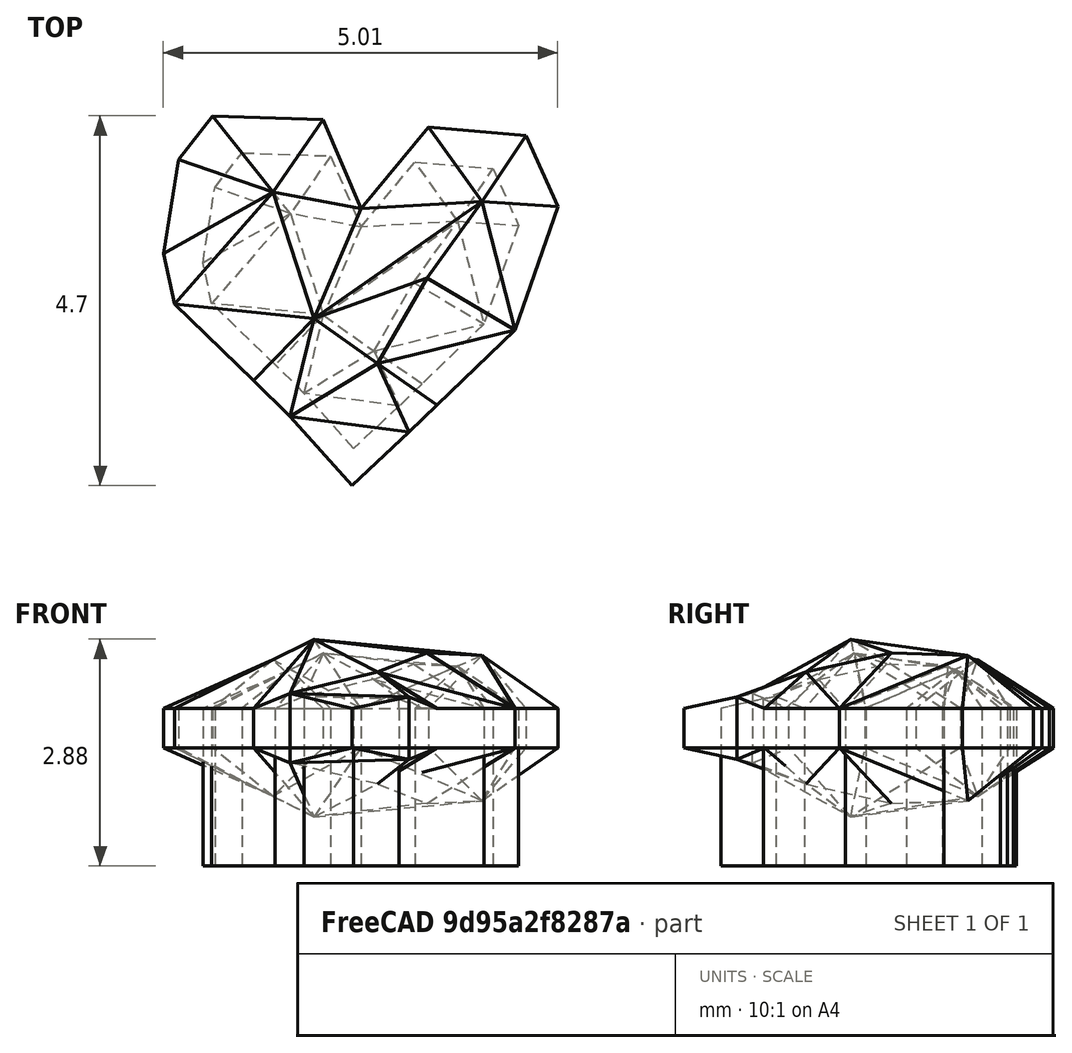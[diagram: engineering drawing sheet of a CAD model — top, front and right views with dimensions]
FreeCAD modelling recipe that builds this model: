
FCSTD DOCUMENT  (FreeCAD 0.20RUnknown)
Label: heart
License: All rights reserved
LicenseURL: http://en.wikipedia.org/wiki/All_rights_reserved
objects: Part::Feature×5, PartDesign::FeatureBase×3, PartDesign::Body×3, Mesh::Feature×2, Sketcher::SketchObject×2, PartDesign::Pad×2, PartDesign::SubShapeBinder×1, Part::Mirroring×1, PartDesign::Boolean×1
note: 20 computed .brp shape members not serialized (recipe doc carries the construction recipe); baked Part::Feature solids carry a one-line shape summary decoded from their .brp

FEATURE [Mesh::Feature] heart_poly_solid
FEATURE [Part::Feature] heart_poly_solid001
  shape: bbox 5.011 x 4.692 x 0.8774 mm, 41 faces, 0 solids (baked)
FEATURE [Part::Feature] heart_poly_solid001_solid  label="heart_poly_solid001 (Solid)"
  shape: bbox 5.011 x 4.692 x 0.8774 mm, 41 faces (baked)
FEATURE [PartDesign::FeatureBase] BaseFeature
  BaseFeature = -> heart_poly_solid001_solid
FEATURE [PartDesign::SubShapeBinder] Binder
  BindCopyOnChange = 0
  BindMode = 0
  ClaimChildren = false
  Context = -> Body [Binder.]
  Fuse = false
  MakeFace = true
  OffsetFill = false
  OffsetIntersection = false
  OffsetJoinType = 0
  OffsetOpenResult = false
  PartialLoad = false
  Relative = true
  Support = -> [heart_poly_solid001_solid]
  _Version = 2
FEATURE [Sketcher::SketchObject] Sketch
  ExternalGeometry = -> [BaseFeature]
  FullyConstrained = true
  MapMode = 5
  Support = -> [XY_Plane]
  sketch-geometry (15):
    g0: LineSegment StartX=-0.114772 StartY=-2.34626 StartZ=0 EndX=-0.898591 EndY=-1.47426 EndZ=0
    g1: LineSegment StartX=-0.898591 StartY=-1.47426 StartZ=0 EndX=-1.36077 EndY=-1.01687 EndZ=0
    g2: LineSegment StartX=-1.36077 StartY=-1.01687 StartZ=0 EndX=-2.36956 EndY=-0.0446064 EndZ=0
    g3: LineSegment StartX=-2.36956 StartY=-0.0446064 StartZ=0 EndX=-2.50731 EndY=0.598821 EndZ=0
    g4: LineSegment StartX=-2.50731 StartY=0.598821 StartZ=0 EndX=-2.31933 EndY=1.79492 EndZ=0
    g5: LineSegment StartX=-2.31933 StartY=1.79492 StartZ=0 EndX=-1.88677 EndY=2.34557 EndZ=0
    g6: LineSegment StartX=-1.88677 StartY=2.34557 StartZ=0 EndX=-0.480936 EndY=2.29776 EndZ=0
    g7: LineSegment StartX=-0.480936 StartY=2.29776 StartZ=0 EndX=-0.000227809 EndY=1.16775 EndZ=0
    g8: LineSegment StartX=-0.000227809 StartY=1.16775 StartZ=0 EndX=0.860947 EndY=2.20207 EndZ=0
    g9: LineSegment StartX=0.860947 StartY=2.20207 StartZ=0 EndX=2.09803 EndY=2.09499 EndZ=0
    g10: LineSegment StartX=2.09803 StartY=2.09499 StartZ=0 EndX=2.50356 EndY=1.19281 EndZ=0
    g11: LineSegment StartX=2.50356 StartY=1.19281 StartZ=0 EndX=1.95514 EndY=-0.370281 EndZ=0
    g12: LineSegment StartX=1.95514 StartY=-0.370281 StartZ=0 EndX=0.967688 EndY=-1.32256 EndZ=0
    g13: LineSegment StartX=0.967688 StartY=-1.32256 StartZ=0 EndX=0.608669 EndY=-1.67147 EndZ=0
    g14: LineSegment StartX=0.608669 StartY=-1.67147 StartZ=0 EndX=-0.114772 EndY=-2.34626 EndZ=0
  constraints (30):
    c: Coincident(g-17,g0)
    c: Coincident(g0,g-17)
    c: Coincident(g0,g1)
    c: Coincident(g1,g-16)
    c: Coincident(g1,g2)
    c: Coincident(g2,g-15)
    c: Coincident(g2,g3)
    c: Coincident(g3,g-14)
    c: Coincident(g3,g4)
    c: Coincident(g4,g-13)
    c: Coincident(g4,g5)
    c: Coincident(g5,g-12)
    c: Coincident(g5,g6)
    c: Coincident(g6,g-11)
    c: Coincident(g6,g7)
    c: Coincident(g7,g-10)
    c: Coincident(g7,g8)
    c: Coincident(g8,g-9)
    c: Coincident(g8,g9)
    c: Coincident(g9,g-8)
    c: Coincident(g9,g10)
    c: Coincident(g10,g-7)
    c: Coincident(g10,g11)
    c: Coincident(g11,g-6)
    c: Coincident(g11,g12)
    c: Coincident(g12,g-5)
    c: Coincident(g12,g13)
    c: Coincident(g13,g-4)
    c: Coincident(g13,g14)
    c: Coincident(g14,g0)
FEATURE [PartDesign::Pad] Pad
  BaseFeature = -> BaseFeature
  Direction = (0,0,1)
  Length = 0.5
  Length2 = 10
  Profile = -> Sketch
  ReferenceAxis = -> Sketch [N_Axis]
  Reversed = true
  Type = 0
FEATURE [Part::Feature] heart_poly_solid001_solid001  label="heart_mirrored_part"
  shape: bbox 5.011 x 4.692 x 0.8774 mm, 41 faces (baked)
FEATURE [Part::Mirroring] Part__Mirroring  label="heart_mirrored_part (Mirror #1)"
  Base = (0,0,0)
  Normal = (0,0,1)
  Placement = pos=(0,0,-0.5) rot=(0,0,1;0rad)
  Source = -> heart_poly_solid001_solid001
FEATURE [PartDesign::FeatureBase] BaseFeature001
  BaseFeature = -> Part__Mirroring
FEATURE [PartDesign::Body] Body001
  BaseFeature = -> Part__Mirroring
  Group = -> [BaseFeature001]
  Origin = -> Origin001
  Placement = pos=(0,0,-0.5) rot=(0,0,1;0rad)
  Tip = -> BaseFeature001
FEATURE [Mesh::Feature] heart_poly_solid002  label="heart_poly_solid_scaled"
FEATURE [Part::Feature] heart_poly_solid002001  label="heart_poly_solid_scaled_shape"
  shape: bbox 4.009 x 3.753 x 0.702 mm, 41 faces, 0 solids (baked)
FEATURE [Part::Feature] heart_poly_solid002001_solid  label="heart_poly_solid_scaled_shape (Solid)"
  shape: bbox 4.009 x 3.753 x 0.702 mm, 41 faces (baked)
FEATURE [PartDesign::FeatureBase] BaseFeature002
  BaseFeature = -> heart_poly_solid002001_solid
FEATURE [Sketcher::SketchObject] Sketch001
  ExternalGeometry = -> [BaseFeature002]
  FullyConstrained = true
  MapMode = 5
  Support = -> [XY_Plane]
  sketch-geometry (15):
    g0: LineSegment StartX=-0.000182247 StartY=0.9342 StartZ=0 EndX=0.688757 EndY=1.76166 EndZ=0
    g1: LineSegment StartX=0.688757 StartY=1.76166 StartZ=0 EndX=1.67842 EndY=1.67599 EndZ=0
    g2: LineSegment StartX=1.67842 StartY=1.67599 StartZ=0 EndX=2.00285 EndY=0.954248 EndZ=0
    g3: LineSegment StartX=2.00285 StartY=0.954248 StartZ=0 EndX=1.56411 EndY=-0.296224 EndZ=0
    g4: LineSegment StartX=1.56411 StartY=-0.296224 StartZ=0 EndX=0.77415 EndY=-1.05804 EndZ=0
    g5: LineSegment StartX=0.77415 StartY=-1.05804 StartZ=0 EndX=0.486935 EndY=-1.33717 EndZ=0
    g6: LineSegment StartX=0.486935 StartY=-1.33717 StartZ=0 EndX=-0.0918176 EndY=-1.87701 EndZ=0
    g7: LineSegment StartX=-0.0918176 StartY=-1.87701 StartZ=0 EndX=-0.718873 EndY=-1.17941 EndZ=0
    g8: LineSegment StartX=-0.718873 StartY=-1.17941 StartZ=0 EndX=-1.08861 EndY=-0.813493 EndZ=0
    g9: LineSegment StartX=-1.08861 StartY=-0.813493 StartZ=0 EndX=-1.89565 EndY=-0.0356851 EndZ=0
    g10: LineSegment StartX=-1.89565 StartY=-0.0356851 StartZ=0 EndX=-2.00585 EndY=0.479057 EndZ=0
    g11: LineSegment StartX=-2.00585 StartY=0.479057 StartZ=0 EndX=-1.85546 EndY=1.43593 EndZ=0
    g12: LineSegment StartX=-1.85546 StartY=1.43593 StartZ=0 EndX=-1.50942 EndY=1.87646 EndZ=0
    g13: LineSegment StartX=-1.50942 StartY=1.87646 StartZ=0 EndX=-0.384749 EndY=1.8382 EndZ=0
    g14: LineSegment StartX=-0.384749 StartY=1.8382 StartZ=0 EndX=-0.000182247 EndY=0.9342 EndZ=0
  constraints (30):
    c: Coincident(g-5,g0)
    c: Coincident(g0,g-6)
    c: Coincident(g0,g1)
    c: Coincident(g1,g-7)
    c: Coincident(g1,g2)
    c: Coincident(g2,g-8)
    c: Coincident(g2,g3)
    c: Coincident(g3,g-9)
    c: Coincident(g3,g4)
    c: Coincident(g4,g-10)
    c: Coincident(g4,g5)
    c: Coincident(g5,g-11)
    c: Coincident(g5,g6)
    c: Coincident(g6,g-12)
    c: Coincident(g6,g7)
    c: Coincident(g7,g-13)
    c: Coincident(g7,g8)
    c: Coincident(g8,g-14)
    c: Coincident(g8,g9)
    c: Coincident(g9,g-15)
    c: Coincident(g9,g10)
    c: Coincident(g10,g-16)
    c: Coincident(g10,g11)
    c: Coincident(g11,g-17)
    c: Coincident(g11,g12)
    c: Coincident(g12,g-17)
    c: Coincident(g12,g13)
    c: Coincident(g13,g-4)
    c: Coincident(g13,g14)
    c: Coincident(g14,g0)
FEATURE [PartDesign::Pad] Pad001
  BaseFeature = -> BaseFeature002
  Direction = (0,0,1)
  Length = 2
  Length2 = 10
  Profile = -> Sketch001
  ReferenceAxis = -> Sketch001 [N_Axis]
  Reversed = true
  Type = 0
FEATURE [PartDesign::Body] Body002  label="HeartPolyCutout"
  BaseFeature = -> heart_poly_solid002001_solid
  Group = -> [BaseFeature002,Sketch001,Pad001]
  Origin = -> Origin002
  Tip = -> Pad001
FEATURE [PartDesign::Boolean] Boolean
  BaseFeature = -> Pad
  Group = -> [heart_poly_solid002001_solid,Body002]
  Type = 1
FEATURE [PartDesign::Body] Body
  BaseFeature = -> heart_poly_solid001_solid
  Group = -> [BaseFeature,Binder,Sketch,Pad,Boolean]
  Origin = -> Origin
  Tip = -> Boolean
